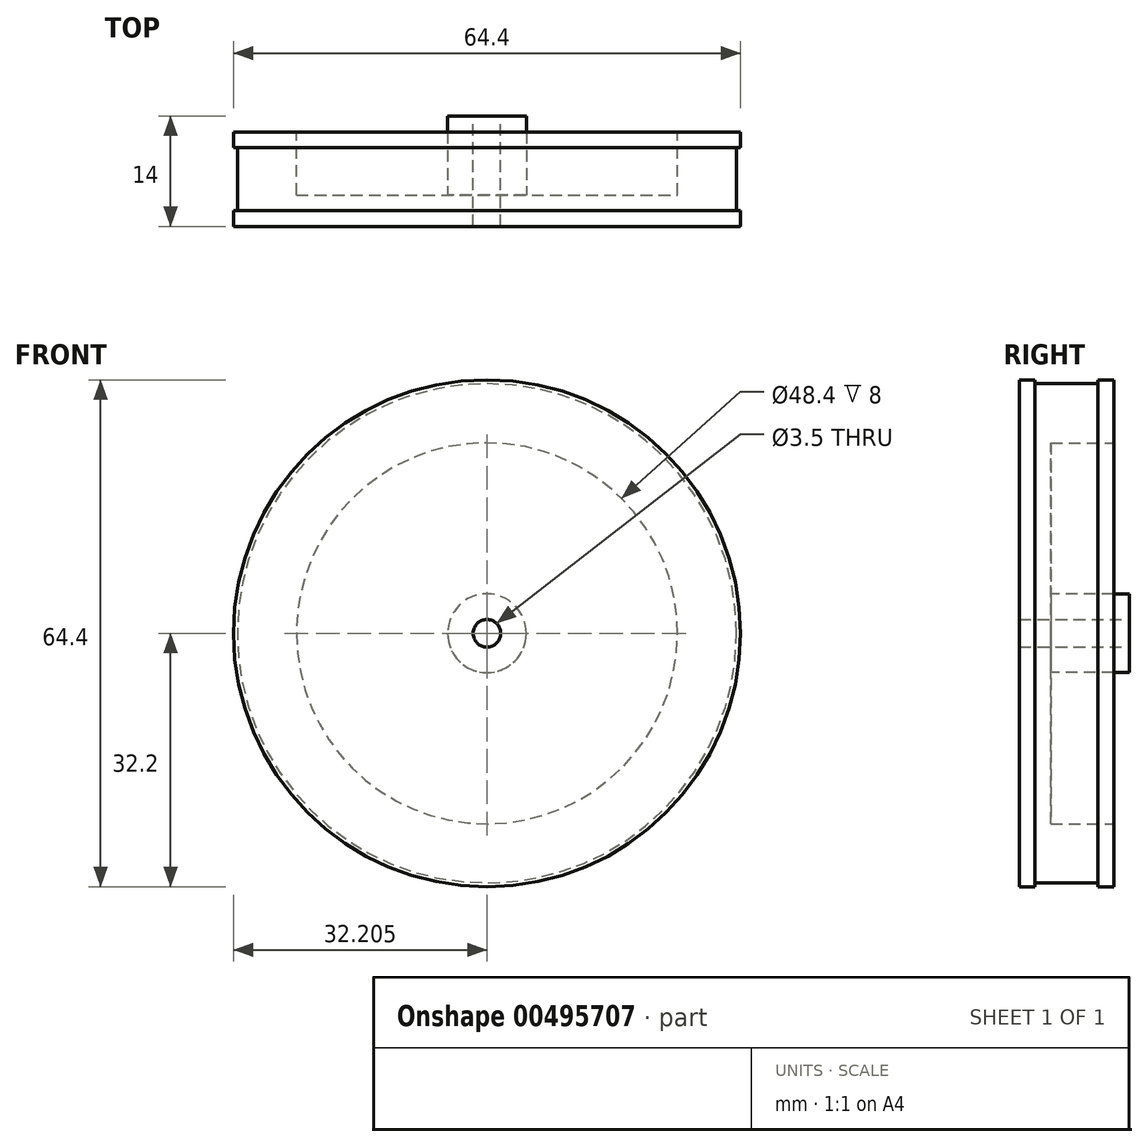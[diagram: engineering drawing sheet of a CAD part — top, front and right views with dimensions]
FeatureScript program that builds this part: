
annotation { "Feature Type Name" : "Feature", "Feature Type Description" : "" }
export const myFeature = defineFeature(function(context is Context, id is Id, definition is map)
    precondition{}
    {
        {
            var Q0;
            Q0=qCreatedBy(makeId("Top.planeOp"),FACE);
            var sketch = newSketch(context, id + "F0", { "sketchPlane" : qUnion([Q0])});
            skLineSegment(sketch, "E0", {"start": v(2.12, 0) * mm, "end": v(34.32, 0) * mm});
            skLineSegment(sketch, "E1", {"start": v(34.32, 0) * mm, "end": v(34.32, 2) * mm});
            skLineSegment(sketch, "E2", {"start": v(34.32, 2) * mm, "end": v(33.82, 2) * mm});
            skLineSegment(sketch, "E3", {"start": v(33.82, 2) * mm, "end": v(33.82, 10) * mm});
            skLineSegment(sketch, "E4", {"start": v(33.82, 10) * mm, "end": v(34.32, 10) * mm});
            skLineSegment(sketch, "E5", {"start": v(34.32, 10) * mm, "end": v(34.32, 12) * mm});
            skLineSegment(sketch, "E6", {"start": v(34.32, 12) * mm, "end": v(26.32, 12) * mm});
            skLineSegment(sketch, "E7", {"start": v(26.32, 12) * mm, "end": v(26.32, 4) * mm});
            skLineSegment(sketch, "E8", {"start": v(26.32, 4) * mm, "end": v(2.12, 4) * mm});
            skLineSegment(sketch, "E9", {"start": v(2.12, 4) * mm, "end": v(2.12, 0) * mm});
            skSolve(sketch);
        }
        {
            var Q0;
            Q0=makeQuery(id+"F0.imprint","IMPRINT",FACE,{"disambiguationData":[TD([[makeQuery(id+"F0.imprint","IMPRINT",EDGE,{"derivedFrom":sQuery(id+"F0.wireOp",EDGE,"E0")}),1.0]])]});
            var Q1;
            Q1=sQuery(id+"F0.wireOp",EDGE,"E9");
            revolve(context, id + "F1", {"entities" : qUnion([Q0]), "axis" : qUnion([Q1]), "revolveType" : RevolveType.FULL});
        }
        {
            var Q0;
            Q0=makeQuery(id+"F1.opRevolve","SWEPT_FACE",FACE,{"disambiguationData":[OSD([sQuery(id+"F0.wireOp",EDGE,"E8")])]});
            var sketch = newSketch(context, id + "F2", { "sketchPlane" : qUnion([Q0])});
            skCircle(sketch, "E10.0.0", {"center": v(-2.12, 0) * mm, "radius": 24.2 * mm});
            skCircle(sketch, "E11", {"center": v(-2.12, 0) * mm, "radius": 5 * mm});
            skSolve(sketch);
        }
        {
            var Q0;
            Q0=makeQuery(id+"F2.imprint","IMPRINT",FACE,{"disambiguationData":[TD([[makeQuery(id+"F2.imprint","IMPRINT",EDGE,{"derivedFrom":sQuery(id+"F2.wireOp",EDGE,"E11")}),1.0]])]});
            extrude(context, id + "F3", {"entities" : qUnion([Q0]), "operationType" : NewBodyOperationType.ADD, "depth" : 10 * mm});
        }
        {
            var Q0;
            Q0=makeQuery(id+"F3.opExtrude","CAP_FACE",FACE,{"disambiguationData":[OSD([sQuery(id+"F2.wireOp",EDGE,"E11")])],"isStart":false});
            var sketch = newSketch(context, id + "F4", { "sketchPlane" : qUnion([Q0])});
            skCircle(sketch, "E12.0.0", {"center": v(-2.12, 0) * mm, "radius": 5 * mm});
            skCircle(sketch, "E13", {"center": v(-2.12, 0) * mm, "radius": 1.75 * mm});
            skSolve(sketch);
        }
        {
            var Q0;
            Q0=makeQuery(id+"F4.imprint","IMPRINT",FACE,{"disambiguationData":[TD([[makeQuery(id+"F4.imprint","IMPRINT",EDGE,{"derivedFrom":sQuery(id+"F4.wireOp",EDGE,"E13")}),1.0]])]});
            extrude(context, id + "F5", {"entities" : qUnion([Q0]), "operationType" : NewBodyOperationType.REMOVE, "oppositeDirection" : true, "depth" : 25 * mm});
        }
    });
